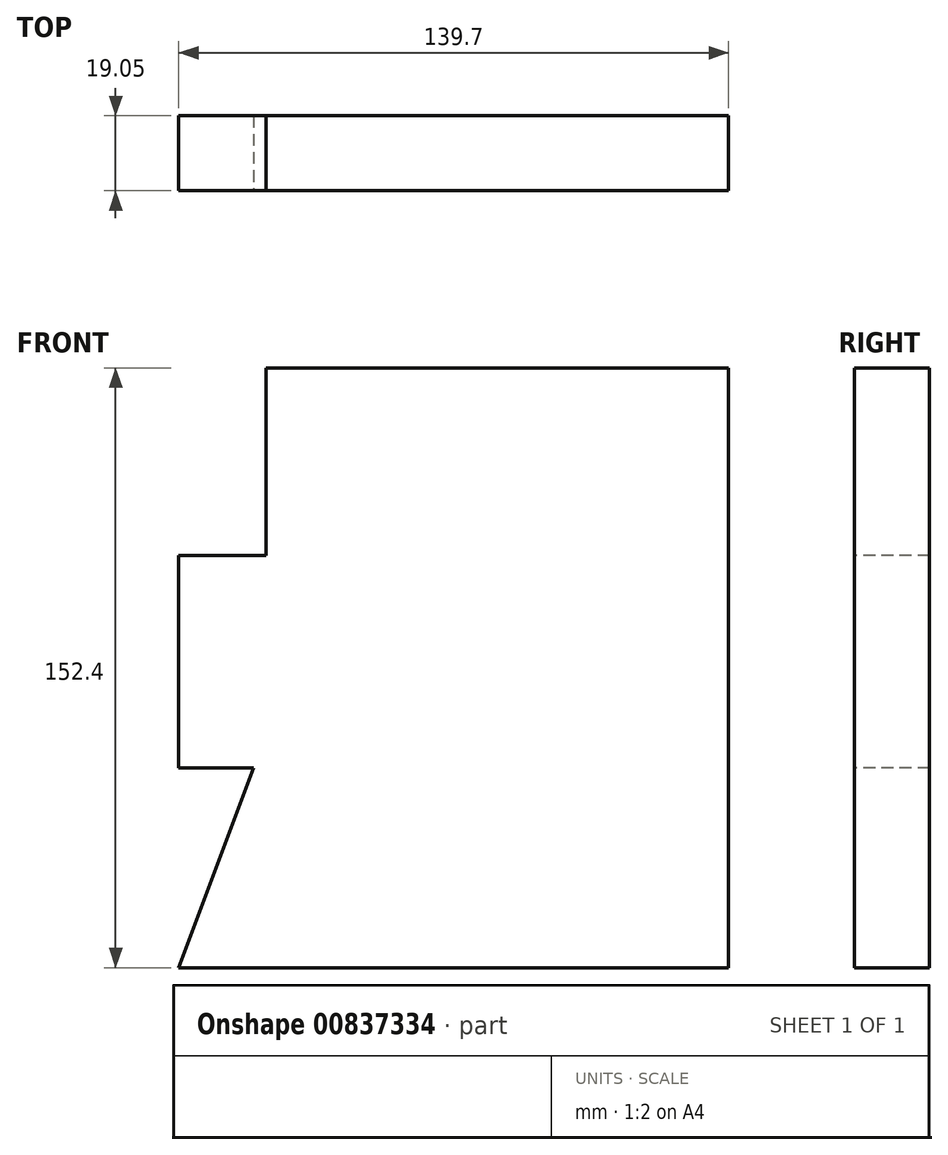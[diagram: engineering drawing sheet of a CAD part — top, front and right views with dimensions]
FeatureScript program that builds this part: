
annotation { "Feature Type Name" : "Feature", "Feature Type Description" : "" }
export const myFeature = defineFeature(function(context is Context, id is Id, definition is map)
    precondition{}
    {
        {
            var Q0;
            Q0=qCreatedBy(makeId("Front.planeOp"),FACE);
            var sketch = newSketch(context, id + "F0", { "sketchPlane" : qUnion([Q0])});
            skLineSegment(sketch, "E0.bottom", {"start": v(0, 0) * mm, "end": v(139.7, 0) * mm});
            skLineSegment(sketch, "E0.top", {"start": v(0, 152.4) * mm, "end": v(139.7, 152.4) * mm});
            skLineSegment(sketch, "E0.left", {"start": v(0, 0) * mm, "end": v(0, 152.4) * mm});
            skLineSegment(sketch, "E0.right", {"start": v(139.7, 0) * mm, "end": v(139.7, 152.4) * mm});
            skSolve(sketch);
        }
        {
            var Q0;
            Q0=makeQuery(id+"F0.imprint","IMPRINT",FACE,{"disambiguationData":[TD([[makeQuery(id+"F0.imprint","IMPRINT",EDGE,{"derivedFrom":sQuery(id+"F0.wireOp",EDGE,"E0.bottom")}),1.0]])]});
            extrude(context, id + "F1", {"entities" : qUnion([Q0]), "depth" : 19.05 * mm, "offsetDistance" : 25.4 * mm});
        }
        {
            var Q0;
            Q0=makeQuery(id+"F1.opExtrude","CAP_FACE",FACE,{"disambiguationData":[OSD([sQuery(id+"F0.wireOp",EDGE,"E0.bottom"),sQuery(id+"F0.wireOp",EDGE,"E0.top"),sQuery(id+"F0.wireOp",EDGE,"E0.left"),sQuery(id+"F0.wireOp",EDGE,"E0.right")])],"isStart":false});
            var sketch = newSketch(context, id + "F2", { "sketchPlane" : qUnion([Q0])});
            skLineSegment(sketch, "E1", {"start": v(0, 104.77) * mm, "end": v(22.22, 104.77) * mm});
            skLineSegment(sketch, "E2", {"start": v(22.22, 104.77) * mm, "end": v(22.22, 152.4) * mm});
            skLineSegment(sketch, "E3", {"start": v(22.22, 152.4) * mm, "end": v(0, 152.4) * mm});
            skLineSegment(sketch, "E4", {"start": v(0, 152.4) * mm, "end": v(0, 104.77) * mm});
            skSolve(sketch);
        }
        {
            var Q0;
            Q0=makeQuery(id+"F2.imprint","IMPRINT",FACE,{"disambiguationData":[TD([[makeQuery(id+"F2.imprint","IMPRINT",EDGE,{"derivedFrom":sQuery(id+"F2.wireOp",EDGE,"E1")}),1.0]])]});
            extrude(context, id + "F3", {"entities" : qUnion([Q0]), "operationType" : NewBodyOperationType.REMOVE, "endBound" : BoundingType.THROUGH_ALL, "oppositeDirection" : true, "depth" : 25.4 * mm, "offsetDistance" : 25.4 * mm});
        }
        {
            var Q0;
            Q0=makeQuery(id+"F1.opExtrude","SWEPT_FACE",FACE,{"disambiguationData":[OSD([sQuery(id+"F0.wireOp",EDGE,"E0.right")])]});
            cPlane(context, id + "F4", {"entities" : qUnion([Q0]), "cplaneType" : CPlaneType.OFFSET, "offset" : 5.5 / 50.8 * mm, "oppositeDirection" : true, "width" : 152.4 * mm, "height" : 152.4 * mm});
        }
        {
            var Q0;
            Q0=makeQuery(id+"F1.opExtrude","CAP_FACE",FACE,{"disambiguationData":[OSD([sQuery(id+"F0.wireOp",EDGE,"E0.bottom"),sQuery(id+"F0.wireOp",EDGE,"E0.top"),sQuery(id+"F0.wireOp",EDGE,"E0.left"),sQuery(id+"F0.wireOp",EDGE,"E0.right")])],"isStart":false});
            var sketch = newSketch(context, id + "F5", { "sketchPlane" : qUnion([Q0])});
            skLineSegment(sketch, "E5", {"start": v(0, 0) * mm, "end": v(19.05, 50.8) * mm});
            skLineSegment(sketch, "E6", {"start": v(19.05, 50.8) * mm, "end": v(0, 50.8) * mm});
            skLineSegment(sketch, "E7", {"start": v(0, 50.8) * mm, "end": v(0, 0) * mm});
            skSolve(sketch);
        }
        {
            var Q0;
            Q0=makeQuery(id+"F5.imprint","IMPRINT",FACE,{"disambiguationData":[TD([[makeQuery(id+"F5.imprint","IMPRINT",EDGE,{"derivedFrom":sQuery(id+"F5.wireOp",EDGE,"E5")}),1.0]])]});
            extrude(context, id + "F6", {"entities" : qUnion([Q0]), "operationType" : NewBodyOperationType.REMOVE, "endBound" : BoundingType.THROUGH_ALL, "oppositeDirection" : true, "depth" : 25.4 * mm, "offsetDistance" : 25.4 * mm});
        }
    });
